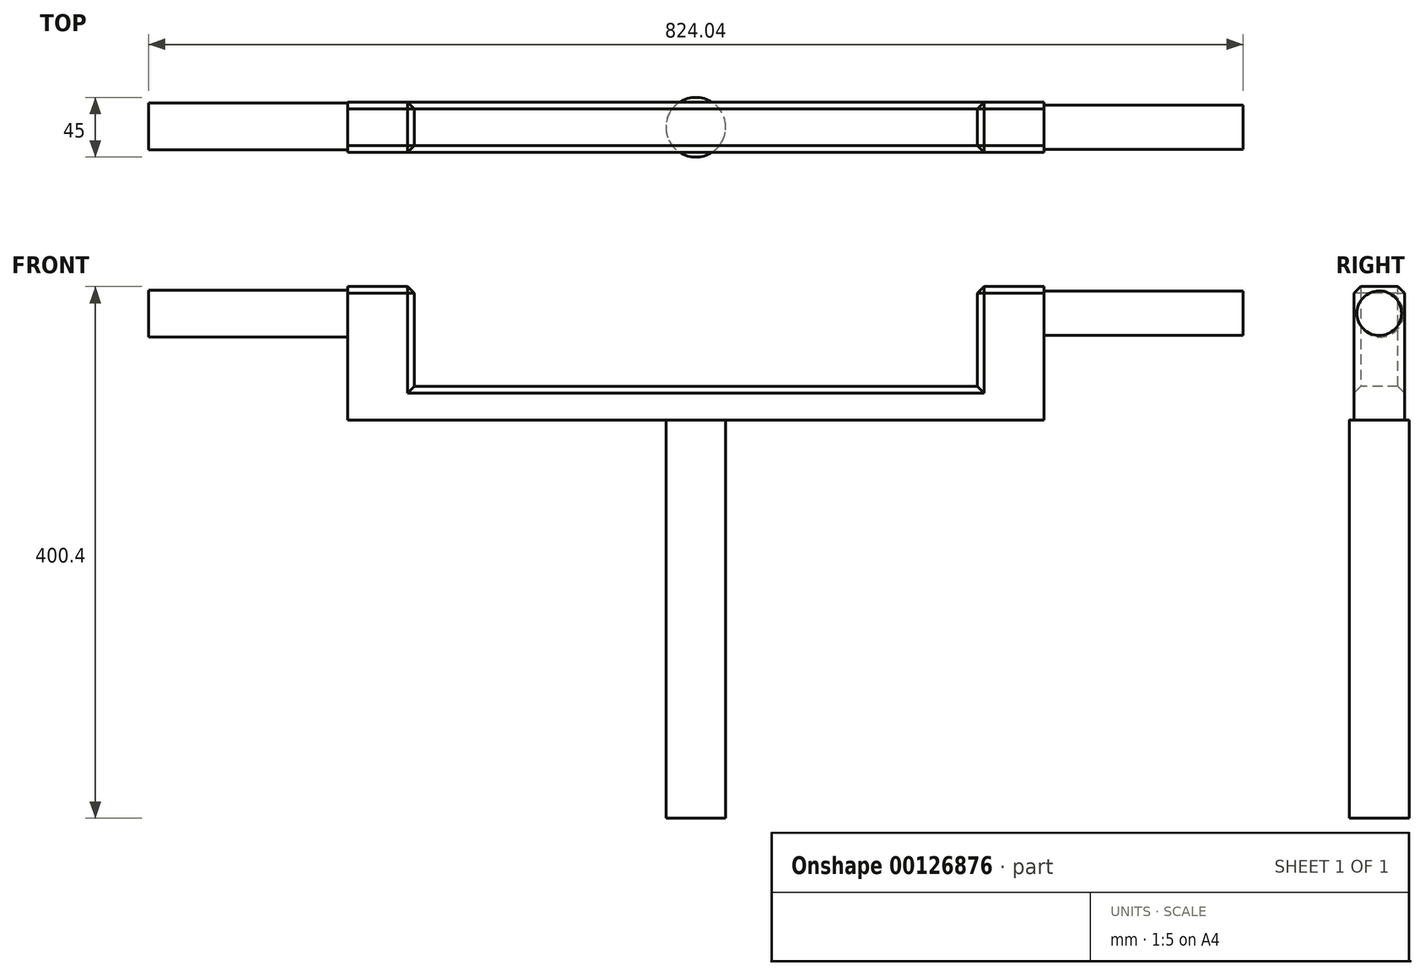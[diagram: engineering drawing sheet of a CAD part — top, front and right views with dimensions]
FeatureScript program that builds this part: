
annotation { "Feature Type Name" : "Feature", "Feature Type Description" : "" }
export const myFeature = defineFeature(function(context is Context, id is Id, definition is map)
    precondition{}
    {
        {
            var Q0;
            Q0=qCreatedBy(makeId("Top.planeOp"),FACE);
            var sketch = newSketch(context, id + "F0", { "sketchPlane" : qUnion([Q0])});
            skCircle(sketch, "E0", {"center": v(-6.66, 15.57) * mm, "radius": 22.5 * mm});
            skSolve(sketch);
        }
        {
            var Q0;
            Q0=makeQuery(id+"F0.imprint","IMPRINT",FACE,{"disambiguationData":[TD([[makeQuery(id+"F0.imprint","IMPRINT",EDGE,{"derivedFrom":sQuery(id+"F0.wireOp",EDGE,"E0")}),1.0]])]});
            extrude(context, id + "F1", {"entities" : qUnion([Q0]), "depth" : 300 * mm});
        }
        {
            var Q0;
            Q0=makeQuery(id+"F1.opExtrude","CAP_FACE",FACE,{"disambiguationData":[OSD([sQuery(id+"F0.wireOp",EDGE,"E0")])],"isStart":false});
            var sketch = newSketch(context, id + "F2", { "sketchPlane" : qUnion([Q0])});
            skLineSegment(sketch, "E1.bottom", {"start": v(5.36, -3.45) * mm, "end": v(-18.68, -3.45) * mm});
            skLineSegment(sketch, "E1.top", {"start": v(5.36, 34.6) * mm, "end": v(-18.68, 34.6) * mm});
            skLineSegment(sketch, "E1.left", {"start": v(5.36, -3.45) * mm, "end": v(5.36, 34.6) * mm});
            skLineSegment(sketch, "E1.right", {"start": v(-18.68, -3.45) * mm, "end": v(-18.68, 34.6) * mm});
            skPoint(sketch, "E1.middle", {"position": v(-6.66, 15.57) * mm});
            skSolve(sketch);
        }
        {
            var Q0;
            Q0=makeQuery(id+"F2.imprint","IMPRINT",FACE,{"disambiguationData":[TD([[makeQuery(id+"F2.imprint","IMPRINT",EDGE,{"derivedFrom":sQuery(id+"F2.wireOp",EDGE,"E1.bottom")}),-1.0]])]});
            extrude(context, id + "F3", {"entities" : qUnion([Q0]), "operationType" : NewBodyOperationType.ADD, "depth" : 25.4 * mm});
        }
        {
            var Q0;
            Q0=makeQuery(id+"F3.opExtrude","SWEPT_FACE",FACE,{"disambiguationData":[OSD([sQuery(id+"F2.wireOp",EDGE,"E1.right")])]});
            var sketch = newSketch(context, id + "F4", { "sketchPlane" : qUnion([Q0])});
            skLineSegment(sketch, "E2.bottom", {"start": v(-34.6, 325.4) * mm, "end": v(3.45, 325.4) * mm});
            skLineSegment(sketch, "E2.top", {"start": v(-34.6, 300) * mm, "end": v(3.45, 300) * mm});
            skLineSegment(sketch, "E2.left", {"start": v(-34.6, 325.4) * mm, "end": v(-34.6, 300) * mm});
            skLineSegment(sketch, "E2.right", {"start": v(3.45, 325.4) * mm, "end": v(3.45, 300) * mm});
            skSolve(sketch);
        }
        {
            var Q0;
            Q0=makeQuery(id+"F4.imprint","IMPRINT",FACE,{"disambiguationData":[TD([[makeQuery(id+"F4.imprint","IMPRINT",EDGE,{"derivedFrom":sQuery(id+"F4.wireOp",EDGE,"E2.bottom")}),1.0]])]});
            extrude(context, id + "F5", {"entities" : qUnion([Q0]), "operationType" : NewBodyOperationType.ADD, "depth" : 250 * mm});
        }
        {
            var Q0;
            Q0=makeQuery(id+"F5.boolean.opBoolean","MERGE",FACE,{"derivedFrom":[makeQuery(id+"F3.opExtrude","CAP_FACE",FACE,{"disambiguationData":[OSD([sQuery(id+"F2.wireOp",EDGE,"E1.bottom"),sQuery(id+"F2.wireOp",EDGE,"E1.top"),sQuery(id+"F2.wireOp",EDGE,"E1.left"),sQuery(id+"F2.wireOp",EDGE,"E1.right")])],"isStart":false}),makeQuery(id+"F5.opExtrude","SWEPT_FACE",FACE,{"disambiguationData":[OSD([sQuery(id+"F4.wireOp",EDGE,"E2.bottom")])]})]});
            var sketch = newSketch(context, id + "F6", { "sketchPlane" : qUnion([Q0])});
            skLineSegment(sketch, "E3.bottom", {"start": v(-268.68, 34.6) * mm, "end": v(-218.68, 34.6) * mm});
            skLineSegment(sketch, "E3.top", {"start": v(-268.68, -3.45) * mm, "end": v(-218.68, -3.45) * mm});
            skLineSegment(sketch, "E3.left", {"start": v(-268.68, 34.6) * mm, "end": v(-268.68, -3.45) * mm});
            skLineSegment(sketch, "E3.right", {"start": v(-218.68, 34.6) * mm, "end": v(-218.68, -3.45) * mm});
            skSolve(sketch);
        }
        {
            var Q0;
            Q0=makeQuery(id+"F6.imprint","IMPRINT",FACE,{"disambiguationData":[TD([[makeQuery(id+"F6.imprint","IMPRINT",EDGE,{"derivedFrom":sQuery(id+"F6.wireOp",EDGE,"E3.bottom")}),1.0]])]});
            extrude(context, id + "F7", {"entities" : qUnion([Q0]), "operationType" : NewBodyOperationType.ADD, "depth" : 75 * mm});
        }
        {
            var Q0;
            Q0=makeQuery(id+"F7.boolean.opBoolean","MERGE",FACE,{"derivedFrom":[makeQuery(id+"F5.opExtrude","CAP_FACE",FACE,{"disambiguationData":[OSD([sQuery(id+"F4.wireOp",EDGE,"E2.bottom"),sQuery(id+"F4.wireOp",EDGE,"E2.top"),sQuery(id+"F4.wireOp",EDGE,"E2.left"),sQuery(id+"F4.wireOp",EDGE,"E2.right")])],"isStart":false}),makeQuery(id+"F7.opExtrude","SWEPT_FACE",FACE,{"disambiguationData":[OSD([sQuery(id+"F6.wireOp",EDGE,"E3.left")])]})]});
            var sketch = newSketch(context, id + "F8", { "sketchPlane" : qUnion([Q0])});
            skCircle(sketch, "E4", {"center": v(-16.25, 380.01) * mm, "radius": 17.58 * mm});
            skSolve(sketch);
        }
        {
            var Q0;
            Q0=makeQuery(id+"F3.opExtrude","SWEPT_FACE",FACE,{"disambiguationData":[OSD([sQuery(id+"F2.wireOp",EDGE,"E1.left")])]});
            var sketch = newSketch(context, id + "F9", { "sketchPlane" : qUnion([Q0])});
            skLineSegment(sketch, "E5.bottom", {"start": v(-3.45, 325.4) * mm, "end": v(34.6, 325.4) * mm});
            skLineSegment(sketch, "E5.top", {"start": v(-3.45, 300) * mm, "end": v(34.6, 300) * mm});
            skLineSegment(sketch, "E5.left", {"start": v(-3.45, 325.4) * mm, "end": v(-3.45, 300) * mm});
            skLineSegment(sketch, "E5.right", {"start": v(34.6, 325.4) * mm, "end": v(34.6, 300) * mm});
            skSolve(sketch);
        }
        {
            var Q0;
            Q0=makeQuery(id+"F9.imprint","IMPRINT",FACE,{"disambiguationData":[TD([[makeQuery(id+"F9.imprint","IMPRINT",EDGE,{"derivedFrom":sQuery(id+"F9.wireOp",EDGE,"E5.bottom")}),-1.0]])]});
            extrude(context, id + "F10", {"entities" : qUnion([Q0]), "operationType" : NewBodyOperationType.ADD, "depth" : 250 * mm});
        }
        {
            var Q0;
            Q0=makeQuery(id+"F10.boolean.opBoolean","MERGE",FACE,{"derivedFrom":[makeQuery(id+"F5.boolean.opBoolean","MERGE",FACE,{"derivedFrom":[makeQuery(id+"F3.opExtrude","CAP_FACE",FACE,{"disambiguationData":[OSD([sQuery(id+"F2.wireOp",EDGE,"E1.bottom"),sQuery(id+"F2.wireOp",EDGE,"E1.top"),sQuery(id+"F2.wireOp",EDGE,"E1.left"),sQuery(id+"F2.wireOp",EDGE,"E1.right")])],"isStart":false}),makeQuery(id+"F5.opExtrude","SWEPT_FACE",FACE,{"disambiguationData":[OSD([sQuery(id+"F4.wireOp",EDGE,"E2.bottom")])]})]}),makeQuery(id+"F10.opExtrude","SWEPT_FACE",FACE,{"disambiguationData":[OSD([sQuery(id+"F9.wireOp",EDGE,"E5.bottom")])]})]});
            var sketch = newSketch(context, id + "F11", { "sketchPlane" : qUnion([Q0])});
            skLineSegment(sketch, "E6.bottom", {"start": v(255.36, 34.6) * mm, "end": v(205.36, 34.6) * mm});
            skLineSegment(sketch, "E6.top", {"start": v(255.36, -3.45) * mm, "end": v(205.36, -3.45) * mm});
            skLineSegment(sketch, "E6.left", {"start": v(255.36, 34.6) * mm, "end": v(255.36, -3.45) * mm});
            skLineSegment(sketch, "E6.right", {"start": v(205.36, 34.6) * mm, "end": v(205.36, -3.45) * mm});
            skSolve(sketch);
        }
        {
            var Q0;
            Q0=makeQuery(id+"F11.imprint","IMPRINT",FACE,{"disambiguationData":[TD([[makeQuery(id+"F11.imprint","IMPRINT",EDGE,{"derivedFrom":sQuery(id+"F11.wireOp",EDGE,"E6.bottom")}),1.0]])]});
            extrude(context, id + "F12", {"entities" : qUnion([Q0]), "operationType" : NewBodyOperationType.ADD, "depth" : 75 * mm});
        }
        {
            var Q0;
            Q0=makeQuery(id+"F12.boolean.opBoolean","MERGE",FACE,{"derivedFrom":[makeQuery(id+"F10.opExtrude","CAP_FACE",FACE,{"disambiguationData":[OSD([sQuery(id+"F9.wireOp",EDGE,"E5.bottom"),sQuery(id+"F9.wireOp",EDGE,"E5.top"),sQuery(id+"F9.wireOp",EDGE,"E5.left"),sQuery(id+"F9.wireOp",EDGE,"E5.right")])],"isStart":false}),makeQuery(id+"F12.opExtrude","SWEPT_FACE",FACE,{"disambiguationData":[OSD([sQuery(id+"F11.wireOp",EDGE,"E6.left")])]})]});
            var sketch = newSketch(context, id + "F13", { "sketchPlane" : qUnion([Q0])});
            skCircle(sketch, "E7", {"center": v(15.57, 380.4) * mm, "radius": 16.77 * mm});
            skPoint(sketch, "E7.centerSnap0", {"position": v(15.57, 400.4) * mm});
            skSolve(sketch);
        }
        {
            var Q0;
            Q0=makeQuery(id+"F13.imprint","IMPRINT",FACE,{"disambiguationData":[TD([[makeQuery(id+"F13.imprint","IMPRINT",EDGE,{"derivedFrom":sQuery(id+"F13.wireOp",EDGE,"E7")}),1.0]])]});
            extrude(context, id + "F14", {"entities" : qUnion([Q0]), "operationType" : NewBodyOperationType.ADD, "depth" : 150 * mm});
        }
        {
            var Q0;
            Q0=makeQuery(id+"F8.imprint","IMPRINT",FACE,{"disambiguationData":[TD([[makeQuery(id+"F8.imprint","IMPRINT",EDGE,{"derivedFrom":sQuery(id+"F8.wireOp",EDGE,"E4")}),1.0]])]});
            extrude(context, id + "F15", {"entities" : qUnion([Q0]), "operationType" : NewBodyOperationType.ADD, "depth" : 150 * mm});
        }
        {
            var Q0;
            Q0=makeQuery(id+"F10.boolean.opBoolean","MERGE",EDGE,{"derivedFrom":[makeQuery(id+"F5.boolean.opBoolean","MERGE",EDGE,{"derivedFrom":[makeQuery(id+"F3.opExtrude","CAP_EDGE",EDGE,{"disambiguationData":[OSD([sQuery(id+"F2.wireOp",EDGE,"E1.bottom")])],"isStart":false}),makeQuery(id+"F5.opExtrude","SWEPT_EDGE",EDGE,{"disambiguationData":[OSD([sQuery(id+"F4.wireOp",EDGE,"E2.bottom"),sQuery(id+"F4.wireOp",EDGE,"E2.right")])]})]}),makeQuery(id+"F10.opExtrude","SWEPT_EDGE",EDGE,{"disambiguationData":[OSD([sQuery(id+"F9.wireOp",EDGE,"E5.bottom"),sQuery(id+"F9.wireOp",EDGE,"E5.left")])]})]});
            var Q1;
            Q1=makeQuery(id+"F10.boolean.opBoolean","MERGE",EDGE,{"derivedFrom":[makeQuery(id+"F5.boolean.opBoolean","MERGE",EDGE,{"derivedFrom":[makeQuery(id+"F3.opExtrude","CAP_EDGE",EDGE,{"disambiguationData":[OSD([sQuery(id+"F2.wireOp",EDGE,"E1.top")])],"isStart":false}),makeQuery(id+"F5.opExtrude","SWEPT_EDGE",EDGE,{"disambiguationData":[OSD([sQuery(id+"F4.wireOp",EDGE,"E2.bottom"),sQuery(id+"F4.wireOp",EDGE,"E2.left")])]})]}),makeQuery(id+"F10.opExtrude","SWEPT_EDGE",EDGE,{"disambiguationData":[OSD([sQuery(id+"F9.wireOp",EDGE,"E5.bottom"),sQuery(id+"F9.wireOp",EDGE,"E5.right")])]})]});
            var Q2;
            Q2=makeQuery(id+"F7.opExtrude","SWEPT_EDGE",EDGE,{"disambiguationData":[OSD([sQuery(id+"F2.wireOp",EDGE,"E1.bottom"),sQuery(id+"F4.wireOp",EDGE,"E2.bottom"),sQuery(id+"F4.wireOp",EDGE,"E2.right"),sQuery(id+"F6.wireOp",EDGE,"E3.top"),sQuery(id+"F6.wireOp",EDGE,"E3.right")])]});
            var Q3;
            Q3=makeQuery(id+"F7.opExtrude","SWEPT_EDGE",EDGE,{"disambiguationData":[OSD([sQuery(id+"F2.wireOp",EDGE,"E1.top"),sQuery(id+"F4.wireOp",EDGE,"E2.bottom"),sQuery(id+"F4.wireOp",EDGE,"E2.left"),sQuery(id+"F6.wireOp",EDGE,"E3.bottom"),sQuery(id+"F6.wireOp",EDGE,"E3.right")])]});
            var Q4;
            Q4=makeQuery(id+"F12.opExtrude","SWEPT_EDGE",EDGE,{"disambiguationData":[OSD([sQuery(id+"F2.wireOp",EDGE,"E1.bottom"),sQuery(id+"F4.wireOp",EDGE,"E2.bottom"),sQuery(id+"F4.wireOp",EDGE,"E2.right"),sQuery(id+"F9.wireOp",EDGE,"E5.bottom"),sQuery(id+"F9.wireOp",EDGE,"E5.left"),sQuery(id+"F11.wireOp",EDGE,"E6.top"),sQuery(id+"F11.wireOp",EDGE,"E6.right")])]});
            var Q5;
            Q5=makeQuery(id+"F12.opExtrude","SWEPT_EDGE",EDGE,{"disambiguationData":[OSD([sQuery(id+"F2.wireOp",EDGE,"E1.top"),sQuery(id+"F4.wireOp",EDGE,"E2.bottom"),sQuery(id+"F4.wireOp",EDGE,"E2.left"),sQuery(id+"F9.wireOp",EDGE,"E5.bottom"),sQuery(id+"F9.wireOp",EDGE,"E5.right"),sQuery(id+"F11.wireOp",EDGE,"E6.bottom"),sQuery(id+"F11.wireOp",EDGE,"E6.right")])]});
            var Q6;
            Q6=makeQuery(id+"F12.opExtrude","CAP_EDGE",EDGE,{"disambiguationData":[OSD([sQuery(id+"F11.wireOp",EDGE,"E6.right")])],"isStart":false});
            var Q7;
            Q7=makeQuery(id+"F7.opExtrude","CAP_EDGE",EDGE,{"disambiguationData":[OSD([sQuery(id+"F6.wireOp",EDGE,"E3.right")])],"isStart":false});
            var Q8;
            Q8=makeQuery(id+"F7.opExtrude","CAP_EDGE",EDGE,{"disambiguationData":[OSD([sQuery(id+"F6.wireOp",EDGE,"E3.top")])],"isStart":false});
            var Q9;
            Q9=makeQuery(id+"F7.opExtrude","CAP_EDGE",EDGE,{"disambiguationData":[OSD([sQuery(id+"F6.wireOp",EDGE,"E3.bottom")])],"isStart":false});
            var Q10;
            Q10=makeQuery(id+"F12.opExtrude","CAP_EDGE",EDGE,{"disambiguationData":[OSD([sQuery(id+"F11.wireOp",EDGE,"E6.bottom")])],"isStart":false});
            var Q11;
            Q11=makeQuery(id+"F12.opExtrude","CAP_EDGE",EDGE,{"disambiguationData":[OSD([sQuery(id+"F11.wireOp",EDGE,"E6.top")])],"isStart":false});
            chamfer(context, id + "F16", {"entities" : qUnion([Q0, Q1, Q2, Q3, Q4, Q5, Q6, Q7, Q8, Q9, Q10, Q11]), "width" : 5.08 * mm, "tangentPropagation" : true});
        }
    });
